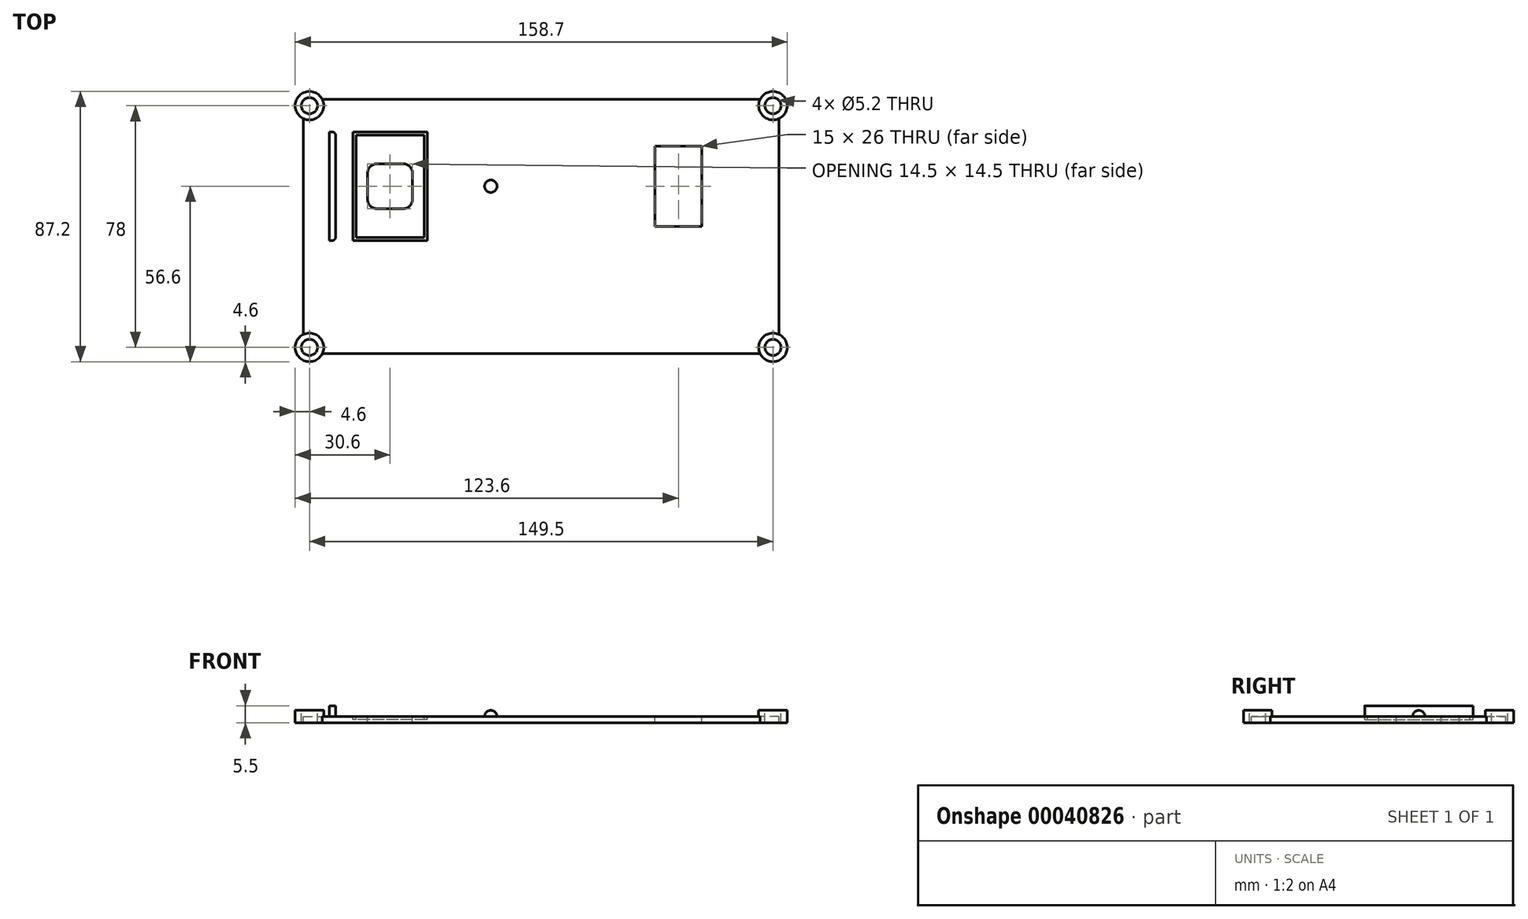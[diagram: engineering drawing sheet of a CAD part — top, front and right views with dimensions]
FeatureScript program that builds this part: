
annotation { "Feature Type Name" : "Feature", "Feature Type Description" : "" }
export const myFeature = defineFeature(function(context is Context, id is Id, definition is map)
    precondition{}
    {
        {
            var Q0;
            Q0=qCreatedBy(makeId("Top.planeOp"),FACE);
            var sketch = newSketch(context, id + "F0", { "sketchPlane" : qUnion([Q0])});
            skLineSegment(sketch, "E0.rect.bottom", {"start": v(76.75, -41) * mm, "end": v(-76.75, -41) * mm});
            skLineSegment(sketch, "E0.rect.top", {"start": v(76.75, 41) * mm, "end": v(-76.75, 41) * mm});
            skLineSegment(sketch, "E0.rect.left", {"start": v(76.75, -41) * mm, "end": v(76.75, 41) * mm});
            skLineSegment(sketch, "E0.rect.right", {"start": v(-76.75, -41) * mm, "end": v(-76.75, 41) * mm});
            skPoint(sketch, "E0.rect.middle", {"position": v(0, 0) * mm});
            skSolve(sketch);
        }
        {
            var Q0;
            Q0=makeQuery(id+"F0.imprint","IMPRINT",FACE,{"disambiguationData":[TD([[makeQuery(id+"F0.imprint","IMPRINT",EDGE,{"derivedFrom":sQuery(id+"F0.wireOp",EDGE,"E0.rect.bottom")}),-1.0]])]});
            extrude(context, id + "F1", {"entities" : qUnion([Q0]), "depth" : 2 * mm});
        }
        {
            var Q0;
            Q0=makeQuery(id+"F1.opExtrude","CAP_FACE",FACE,{"disambiguationData":[OSD([sQuery(id+"F0.wireOp",EDGE,"E0.rect.bottom"),sQuery(id+"F0.wireOp",EDGE,"E0.rect.top"),sQuery(id+"F0.wireOp",EDGE,"E0.rect.left"),sQuery(id+"F0.wireOp",EDGE,"E0.rect.right")])],"isStart":false});
            var sketch = newSketch(context, id + "F2", { "sketchPlane" : qUnion([Q0])});
            skLineSegment(sketch, "E1", {"start": v(76.75, 41) * mm, "end": v(36.75, 41) * mm, "construction": true});
            skLineSegment(sketch, "E2", {"start": v(36.75, 41) * mm, "end": v(36.75, 26) * mm, "construction": true});
            skLineSegment(sketch, "E3.bottom", {"start": v(36.75, 26) * mm, "end": v(51.75, 26) * mm});
            skLineSegment(sketch, "E3.top", {"start": v(36.75, 0) * mm, "end": v(51.75, 0) * mm});
            skLineSegment(sketch, "E3.left", {"start": v(36.75, 26) * mm, "end": v(36.75, 0) * mm});
            skLineSegment(sketch, "E3.right", {"start": v(51.75, 26) * mm, "end": v(51.75, 0) * mm});
            skLineSegment(sketch, "E4", {"start": v(-76.75, 41) * mm, "end": v(-48.75, 41) * mm, "construction": true});
            skLineSegment(sketch, "E5", {"start": v(-48.75, 41) * mm, "end": v(-48.75, 13) * mm, "construction": true});
            skLineSegment(sketch, "E6.rect.bottom", {"start": v(-56, 5.75) * mm, "end": v(-41.5, 5.75) * mm});
            skLineSegment(sketch, "E6.rect.top", {"start": v(-56, 20.25) * mm, "end": v(-41.5, 20.25) * mm});
            skLineSegment(sketch, "E6.rect.left", {"start": v(-56, 5.75) * mm, "end": v(-56, 20.25) * mm});
            skLineSegment(sketch, "E6.rect.right", {"start": v(-41.5, 5.75) * mm, "end": v(-41.5, 20.25) * mm});
            skPoint(sketch, "E6.rect.middle", {"position": v(-48.75, 13) * mm});
            skSolve(sketch);
        }
        {
            var Q0;
            Q0 = qSketchRegion(id + "F2", true);
            extrude(context, id + "F3", {"entities" : qUnion([Q0]), "operationType" : NewBodyOperationType.REMOVE, "endBound" : BoundingType.THROUGH_ALL, "oppositeDirection" : true, "depth" : 25 * mm});
        }
        {
            var Q0;
            Q0=makeQuery(id+"F1.opExtrude","CAP_FACE",FACE,{"disambiguationData":[OSD([sQuery(id+"F0.wireOp",EDGE,"E0.rect.bottom"),sQuery(id+"F0.wireOp",EDGE,"E0.rect.top"),sQuery(id+"F0.wireOp",EDGE,"E0.rect.left"),sQuery(id+"F0.wireOp",EDGE,"E0.rect.right")])],"isStart":false});
            var sketch = newSketch(context, id + "F4", { "sketchPlane" : qUnion([Q0])});
            skPoint(sketch, "E7.0", {"position": v(-48.75, 13) * mm});
            skLineSegment(sketch, "E8", {"start": v(-48.75, 13) * mm, "end": v(-16.25, 13) * mm, "construction": true});
            skCircle(sketch, "E9", {"center": v(-16.25, 13) * mm, "radius": 2 * mm});
            skLineSegment(sketch, "E10", {"start": v(-16.25, 13) * mm, "end": v(36.75, 13) * mm, "construction": true});
            skLineSegment(sketch, "E11", {"start": v(0, 0) * mm, "end": v(-5.67, 0) * mm, "construction": true});
            skLineSegment(sketch, "E12", {"start": v(0, 0) * mm, "end": v(0, 4.37) * mm, "construction": true});
            skSolve(sketch);
        }
        {
            var Q0;
            Q0 = qSketchRegion(id + "F4", true);
            extrude(context, id + "F5", {"entities" : qUnion([Q0]), "operationType" : NewBodyOperationType.ADD, "depth" : 2 * mm});
        }
        {
            var Q0;
            Q0=makeQuery(id+"F5.opExtrude","CAP_EDGE",EDGE,{"disambiguationData":[OSD([sQuery(id+"F4.wireOp",EDGE,"E9")])],"isStart":false});
            var Q1;
            Q1=makeQuery(id+"F3.boolean.opBoolean","COPY",EDGE,{"derivedFrom":makeQuery(id+"F3.opExtrude","SWEPT_EDGE",EDGE,{"disambiguationData":[OSD([sQuery(id+"F2.wireOp",EDGE,"0353079d-4cbf-481e-bf5c-13c4c47056ee.top"),sQuery(id+"F2.wireOp",EDGE,"0353079d-4cbf-481e-bf5c-13c4c47056ee.right")])]})});
            var Q2;
            Q2=makeQuery(id+"F3.boolean.opBoolean","COPY",EDGE,{"derivedFrom":makeQuery(id+"F3.opExtrude","SWEPT_EDGE",EDGE,{"disambiguationData":[OSD([sQuery(id+"F2.wireOp",EDGE,"2b1e2a3c-eb79-4765-ba8c-ccc48f389b02.top"),sQuery(id+"F2.wireOp",EDGE,"2b1e2a3c-eb79-4765-ba8c-ccc48f389b02.right")])]})});
            var Q3;
            Q3=makeQuery(id+"F3.boolean.opBoolean","COPY",EDGE,{"derivedFrom":makeQuery(id+"F3.opExtrude","SWEPT_EDGE",EDGE,{"disambiguationData":[OSD([sQuery(id+"F2.wireOp",EDGE,"22e8d83c-65a5-4341-b0df-a53ec006c7a9.top"),sQuery(id+"F2.wireOp",EDGE,"22e8d83c-65a5-4341-b0df-a53ec006c7a9.right")])]})});
            var Q4;
            Q4=makeQuery(id+"F3.boolean.opBoolean","COPY",EDGE,{"derivedFrom":makeQuery(id+"F3.opExtrude","SWEPT_EDGE",EDGE,{"disambiguationData":[OSD([sQuery(id+"F2.wireOp",EDGE,"b1417015-1773-44c1-9ccd-ac1f378505c8.top"),sQuery(id+"F2.wireOp",EDGE,"b1417015-1773-44c1-9ccd-ac1f378505c8.right")])]})});
            var Q5;
            Q5=makeQuery(id+"F5.opExtrude","SWEPT_EDGE",EDGE,{"disambiguationData":[OSD([sQuery(id+"F4.wireOp",EDGE,"ddfcbf99-8b9a-41d4-8a1f-5541448641cc.bottom"),sQuery(id+"F4.wireOp",EDGE,"ddfcbf99-8b9a-41d4-8a1f-5541448641cc.right")])]});
            var Q6;
            Q6=makeQuery(id+"F5.opExtrude","SWEPT_EDGE",EDGE,{"disambiguationData":[OSD([sQuery(id+"F4.wireOp",EDGE,"bf0b263f-b386-4a39-b5c8-11d83e78f4173.MirrorCS"),sQuery(id+"F4.wireOp",EDGE,"bf0b263f-b386-4a39-b5c8-11d83e78f4177.MirrorCS")])]});
            var Q7;
            Q7=makeQuery(id+"F5.opExtrude","SWEPT_EDGE",EDGE,{"disambiguationData":[OSD([sQuery(id+"F4.wireOp",EDGE,"b74cfe65-8689-46ba-a092-59856babf5d42.MirrorCS"),sQuery(id+"F4.wireOp",EDGE,"b74cfe65-8689-46ba-a092-59856babf5d415.MirrorCS")])]});
            var Q8;
            Q8=makeQuery(id+"F5.opExtrude","SWEPT_EDGE",EDGE,{"disambiguationData":[OSD([sQuery(id+"F4.wireOp",EDGE,"b74cfe65-8689-46ba-a092-59856babf5d45.MirrorCS"),sQuery(id+"F4.wireOp",EDGE,"b74cfe65-8689-46ba-a092-59856babf5d410.MirrorCS")])]});
            fillet(context, id + "F6", {"entities" : qUnion([Q0, Q1, Q2, Q3, Q4, Q5, Q6, Q7, Q8]), "radius" : 2 * mm, "tangentPropagation" : true, "allowEdgeOverflow" : false});
        }
        {
            var Q0;
            Q0=makeQuery(id+"F2.imprint","IMPRINT",FACE,{"disambiguationData":[TD([[makeQuery(id+"F2.imprint","IMPRINT",EDGE,{"derivedFrom":sQuery(id+"F2.wireOp",EDGE,"E3.bottom")}),1.0]])]});
            var sketch = newSketch(context, id + "F7", { "sketchPlane" : qUnion([Q0])});
            skPoint(sketch, "E13.0", {"position": v(-48.75, 13) * mm});
            skLineSegment(sketch, "E14.rect.bottom", {"start": v(-36.75, -4.5) * mm, "end": v(-60.75, -4.5) * mm});
            skLineSegment(sketch, "E14.rect.top", {"start": v(-36.75, 30.5) * mm, "end": v(-60.75, 30.5) * mm});
            skLineSegment(sketch, "E14.rect.left", {"start": v(-36.75, -4.5) * mm, "end": v(-36.75, 30.5) * mm});
            skLineSegment(sketch, "E14.rect.right", {"start": v(-60.75, -4.5) * mm, "end": v(-60.75, 30.5) * mm});
            skLineSegment(sketch, "E15.0", {"start": v(-37.75, 29.5) * mm, "end": v(-59.75, 29.5) * mm});
            skLineSegment(sketch, "E15.1", {"start": v(-37.75, -3.5) * mm, "end": v(-37.75, 29.5) * mm});
            skLineSegment(sketch, "E15.2", {"start": v(-37.75, -3.5) * mm, "end": v(-59.75, -3.5) * mm});
            skLineSegment(sketch, "E15.3", {"start": v(-59.75, -3.5) * mm, "end": v(-59.75, 29.5) * mm});
            skSolve(sketch);
        }
        {
            var Q0;
            Q0 = qSketchRegion(id + "F7", true);
            extrude(context, id + "F8", {"entities" : qUnion([Q0]), "operationType" : NewBodyOperationType.REMOVE, "oppositeDirection" : true, "depth" : 1 * mm});
        }
        {
            var Q0;
            Q0=makeQuery(id+"F2.imprint","IMPRINT",FACE,{"disambiguationData":[TD([[makeQuery(id+"F2.imprint","IMPRINT",EDGE,{"derivedFrom":sQuery(id+"F2.wireOp",EDGE,"E3.bottom")}),1.0]])]});
            cPlane(context, id + "F9", {"entities" : qUnion([Q0]), "cplaneType" : CPlaneType.OFFSET, "offset" : 2 * mm, "width" : 150 * mm, "height" : 150 * mm});
        }
        {
            var Q0;
            Q0=qCreatedBy(id+"F9.planeOp",FACE);
            var sketch = newSketch(context, id + "F10", { "sketchPlane" : qUnion([Q0])});
            skLineSegment(sketch, "E16.0", {"start": v(-76.75, -41) * mm, "end": v(-76.75, 41) * mm, "construction": true});
            skLineSegment(sketch, "E17.0", {"start": v(76.75, -41) * mm, "end": v(-76.75, -41) * mm, "construction": true});
            skLineSegment(sketch, "E18.0", {"start": v(76.75, -41) * mm, "end": v(76.75, 41) * mm, "construction": true});
            skLineSegment(sketch, "E19.0", {"start": v(76.75, 41) * mm, "end": v(-76.75, 41) * mm, "construction": true});
            skCircle(sketch, "E20", {"center": v(-74.75, 39) * mm, "radius": 2 * mm, "construction": true});
            skLineSegment(sketch, "E21", {"start": v(0, 0) * mm, "end": v(0, 12.74) * mm, "construction": true});
            skLineSegment(sketch, "E22", {"start": v(0, 0) * mm, "end": v(-13.23, 0) * mm, "construction": true});
            skCircle(sketch, "E23", {"center": v(-74.75, 39) * mm, "radius": 4.6 * mm});
            skCircle(sketch, "E24", {"center": v(-74.75, 39) * mm, "radius": 2.6 * mm});
            skLineSegment(sketch, "E25", {"start": v(-79.35, 39) * mm, "end": v(-77.35, 39) * mm, "construction": true});
            skCircle(sketch, "E26.MirrorC", {"center": v(74.75, 39) * mm, "radius": 4.6 * mm});
            skCircle(sketch, "E27.MirrorC", {"center": v(74.75, 39) * mm, "radius": 2.6 * mm});
            skCircle(sketch, "E28.MirrorC", {"center": v(-74.75, -39) * mm, "radius": 4.6 * mm});
            skCircle(sketch, "E29.MirrorC", {"center": v(-74.75, -39) * mm, "radius": 2.6 * mm});
            skCircle(sketch, "E30.MirrorC", {"center": v(74.75, -39) * mm, "radius": 4.6 * mm});
            skCircle(sketch, "E31.MirrorC", {"center": v(74.75, -39) * mm, "radius": 2.6 * mm});
            skSolve(sketch);
        }
        {
            var Q0;
            Q0 = qSketchRegion(id + "F10", true);
            extrude(context, id + "F11", {"entities" : qUnion([Q0]), "operationType" : NewBodyOperationType.ADD, "oppositeDirection" : true, "depth" : 4 * mm});
        }
        {
            var Q0;
            Q0=makeQuery(id+"F11.opExtrude","CAP_FACE",FACE,{"disambiguationData":[OSD([sQuery(id+"F10.wireOp",EDGE,"E23"),sQuery(id+"F10.wireOp",EDGE,"E24")])],"isStart":true});
            var sketch = newSketch(context, id + "F12", { "sketchPlane" : qUnion([Q0])});
            skCircle(sketch, "E32.0", {"center": v(-74.75, 39) * mm, "radius": 2.6 * mm});
            skCircle(sketch, "E33.0", {"center": v(74.75, 39) * mm, "radius": 2.6 * mm});
            skCircle(sketch, "E34.0", {"center": v(-74.75, -39) * mm, "radius": 2.6 * mm});
            skCircle(sketch, "E35.0", {"center": v(74.75, -39) * mm, "radius": 2.6 * mm});
            skSolve(sketch);
        }
        {
            var Q0;
            Q0 = qSketchRegion(id + "F12", true);
            extrude(context, id + "F13", {"entities" : qUnion([Q0]), "operationType" : NewBodyOperationType.REMOVE, "endBound" : BoundingType.THROUGH_ALL, "oppositeDirection" : true, "depth" : 25 * mm});
        }
        {
            var Q0;
            Q0=qCreatedBy(id+"F9.planeOp",FACE);
            var sketch = newSketch(context, id + "F14", { "sketchPlane" : qUnion([Q0])});
            skLineSegment(sketch, "E36.0", {"start": v(-60.75, -4.5) * mm, "end": v(-60.75, 30.5) * mm, "construction": true});
            skLineSegment(sketch, "E37", {"start": v(-60.75, 30.5) * mm, "end": v(-66.35, 30.5) * mm, "construction": true});
            skLineSegment(sketch, "E38.bottom", {"start": v(-66.35, 30.5) * mm, "end": v(-68.35, 30.5) * mm});
            skLineSegment(sketch, "E38.top", {"start": v(-66.35, -4.5) * mm, "end": v(-68.35, -4.5) * mm});
            skLineSegment(sketch, "E38.left", {"start": v(-66.35, 30.5) * mm, "end": v(-66.35, -4.5) * mm});
            skLineSegment(sketch, "E38.right", {"start": v(-68.35, 30.5) * mm, "end": v(-68.35, -4.5) * mm});
            skSolve(sketch);
        }
        {
            var Q0;
            Q0 = qSketchRegion(id + "F14", true);
            extrude(context, id + "F15", {"entities" : qUnion([Q0]), "operationType" : NewBodyOperationType.ADD, "oppositeDirection" : true, "depth" : 2 * mm, "hasSecondDirection" : true, "secondDirectionOppositeDirection" : false, "secondDirectionDepth" : 1.5 * mm});
        }
        {
            var Q0;
            Q0=makeQuery(id+"F15.opExtrude","SWEPT_EDGE",EDGE,{"disambiguationData":[OSD([sQuery(id+"F14.wireOp",EDGE,"E38.top"),sQuery(id+"F14.wireOp",EDGE,"E38.left")])]});
            var Q1;
            Q1=makeQuery(id+"F15.opExtrude","SWEPT_EDGE",EDGE,{"disambiguationData":[OSD([sQuery(id+"F14.wireOp",EDGE,"E38.bottom"),sQuery(id+"F14.wireOp",EDGE,"E38.left")])]});
            fillet(context, id + "F16", {"entities" : qUnion([Q0, Q1]), "radius" : 1 * mm, "tangentPropagation" : true, "allowEdgeOverflow" : false});
        }
        {
            var Q0;
            Q0=makeQuery(id+"F3.boolean.opBoolean","COPY",EDGE,{"derivedFrom":makeQuery(id+"F3.opExtrude","SWEPT_EDGE",EDGE,{"disambiguationData":[OSD([sQuery(id+"F2.wireOp",EDGE,"E6.rect.top"),sQuery(id+"F2.wireOp",EDGE,"E6.rect.left")])]})});
            var Q1;
            Q1=makeQuery(id+"F3.boolean.opBoolean","COPY",EDGE,{"derivedFrom":makeQuery(id+"F3.opExtrude","SWEPT_EDGE",EDGE,{"disambiguationData":[OSD([sQuery(id+"F2.wireOp",EDGE,"E6.rect.bottom"),sQuery(id+"F2.wireOp",EDGE,"E6.rect.right")])]})});
            var Q2;
            Q2=makeQuery(id+"F3.boolean.opBoolean","COPY",EDGE,{"derivedFrom":makeQuery(id+"F3.opExtrude","SWEPT_EDGE",EDGE,{"disambiguationData":[OSD([sQuery(id+"F2.wireOp",EDGE,"E6.rect.bottom"),sQuery(id+"F2.wireOp",EDGE,"E6.rect.left")])]})});
            var Q3;
            Q3=makeQuery(id+"F3.boolean.opBoolean","COPY",EDGE,{"derivedFrom":makeQuery(id+"F3.opExtrude","SWEPT_EDGE",EDGE,{"disambiguationData":[OSD([sQuery(id+"F2.wireOp",EDGE,"E6.rect.top"),sQuery(id+"F2.wireOp",EDGE,"E6.rect.right")])]})});
            fillet(context, id + "F17", {"entities" : qUnion([Q0, Q1, Q2, Q3]), "radius" : 3 * mm, "tangentPropagation" : true, "allowEdgeOverflow" : false});
        }
    });
